# Revit family: Heat Pump-Rheem-A2W-35kW-Vertical A
name_source: partatom
category: Mechanical Equipment
revit_build: Autodesk Revit 2016 (Build: 20190508_0715(x64)
units: mm (PartAtom-declared; Revit-internal decimal feet)

## family parameters
Always vertical = Yes
Cut with Voids When Loaded = No
OmniClass Number = 23.75.10.21
OmniClass Title = Heat Pumps
Part Type = Normal
Room Calculation Point = No
Round Connector Dimension = Use Radius
Shared = No
Work Plane-Based = No

## types (2) — shared parameters
ApparentLoad_ANZRS = 35 kW
BodyWidth = 807 mm
Height_ANZRS = 1378 mm  [stored 4.521 ft]
InletPipeDiameter = 50 mm  [stored 0.164042 ft]
Length_ANZRS = 1805 mm  [stored 5.92192 ft]
Manufacturer = Rheem
Material_ANZRS = Rheem-Steel-Grey
OutletPipeDiameter = 50 mm  [stored 0.164042 ft]
PipeInsetSide = 145 mm  [stored 0.475722 ft]
PowerFactor_ANZRS = 1
SupportInsetSide = 66 mm  [stored 0.216535 ft]
URL = https://www.rheem.com.au
Voltage_ANZRS = 230 V
Wattage_ANZRS = 35 kW
Width_ANZRS = 807 mm
calcFanGuardDepth = 136 mm
calcInletPipeRadius = 25 mm  [stored 0.082021 ft]
calcOutletPipeRad = 25 mm  [stored 0.082021 ft]

## per-type parameters (varying)
| type | Description | Model | Show Fan Frame |
| 95203500 | Rheem's Commercial Air to Water (A2W) Heat Pump is designed with the commercial user in mind. A truly commercial grade heat pump that delivers hot water at 65°C with a system Coefficient of Performance (COP) up to 4.0. Ducted models are designed to be connected to ducting to convey cold discharge air away from the heat pump air inlet if a sufficient supply of heat energy is not available in the installation area. | Rheem Commercial Air to Water Heat Pump – 35kW Vertical Discharge & Ducted | Yes |
| 95303500 | Rheem's Commercial Air to Water (A2W) Heat Pump is designed with the commercial user in mind. A truly commercial grade heat pump that delivers hot water at 65°C with a system Coefficient of Performance (COP) up to 4.0. Non ducted models are generally designed for outdoor installations. Non ducted models may be installed indoors, without ducting, if a sufficient supply of heat energy is available. | Rheem Commercial Air to Water Heat Pump – 35kW Vertical Discharge & Non Ducted | No |

note: column(s) folded — value = type name in every type: ProductCode_ANZRS

note: [stored X ft] marks values corroborated as IEEE doubles in the binary element streams (Revit-internal decimal feet)

## geometry (parser evidence)
native form markers: Blend x8, Sweep x9
no freeform markers — native parametric forms only
